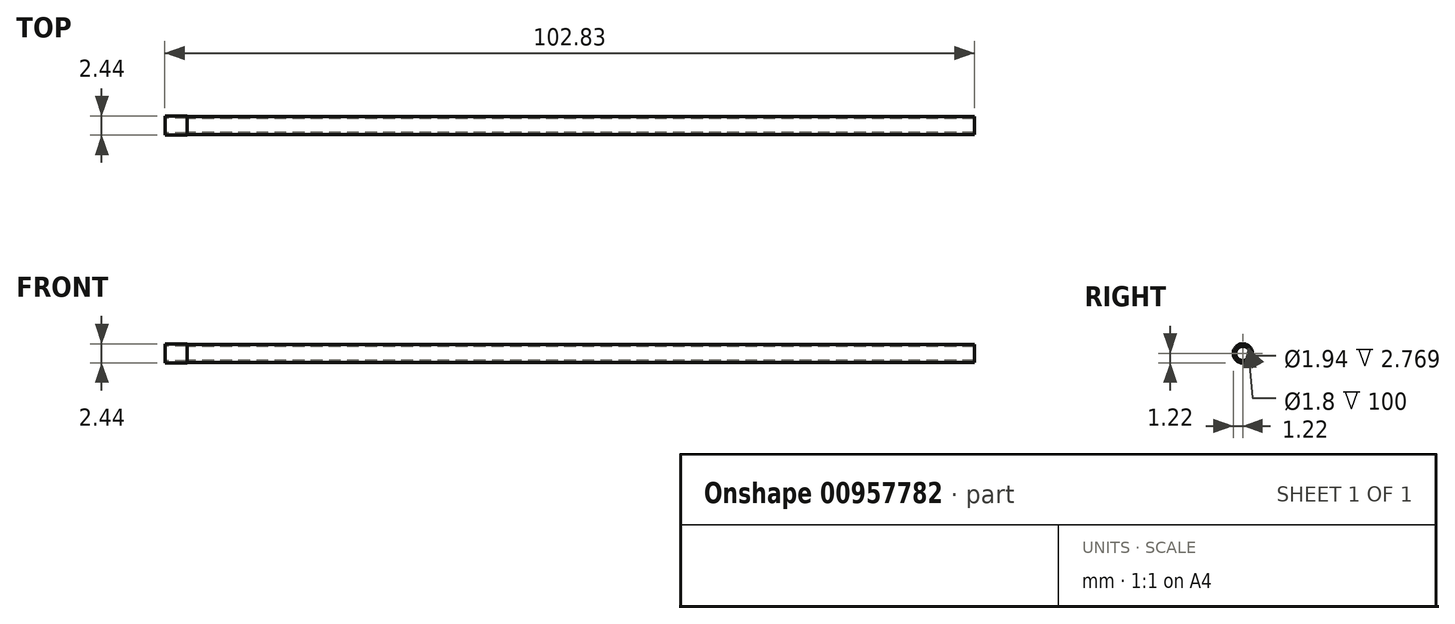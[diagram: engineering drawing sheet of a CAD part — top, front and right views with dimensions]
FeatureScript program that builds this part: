
annotation { "Feature Type Name" : "Feature", "Feature Type Description" : "" }
export const myFeature = defineFeature(function(context is Context, id is Id, definition is map)
    precondition{}
    {
        {
            var Q0;
            Q0=qCreatedBy(makeId("Front.planeOp"),FACE);
            var sketch = newSketch(context, id + "F0", { "sketchPlane" : qUnion([Q0])});
            skLineSegment(sketch, "E0", {"start": v(-6.06, 0) * mm, "end": v(6.25, 0) * mm, "construction": true});
            skLineSegment(sketch, "E1", {"start": v(-5, 0.9) * mm, "end": v(95, 0.9) * mm});
            skLineSegment(sketch, "E2", {"start": v(95, 0.9) * mm, "end": v(95, 1.15) * mm});
            skLineSegment(sketch, "E3", {"start": v(95, 1.15) * mm, "end": v(-5, 1.15) * mm});
            skLineSegment(sketch, "E4", {"start": v(-7.84, 0.97) * mm, "end": v(-5.07, 0.97) * mm});
            skLineSegment(sketch, "E5", {"start": v(-7.84, 0.97) * mm, "end": v(-7.84, 1.22) * mm});
            skLineSegment(sketch, "E6", {"start": v(-7.84, 1.22) * mm, "end": v(-5.04, 1.22) * mm});
            skLineSegment(sketch, "E7", {"start": v(-5.04, 1.22) * mm, "end": v(-5, 1.15) * mm});
            skLineSegment(sketch, "E8", {"start": v(-5, 0.9) * mm, "end": v(-5.07, 0.97) * mm});
            skSolve(sketch);
        }
        {
            var Q0;
            Q0=qSketchRegion(id+"F0",true);
            var Q1;
            Q1=sQuery(id+"F0.wireOp",EDGE,"E0");
            revolve(context, id + "F1", {"surfaceOperationType" : NewSurfaceOperationType.NEW, "entities" : qUnion([Q0]), "axis" : qUnion([Q1]), "revolveType" : RevolveType.FULL});
        }
    });
